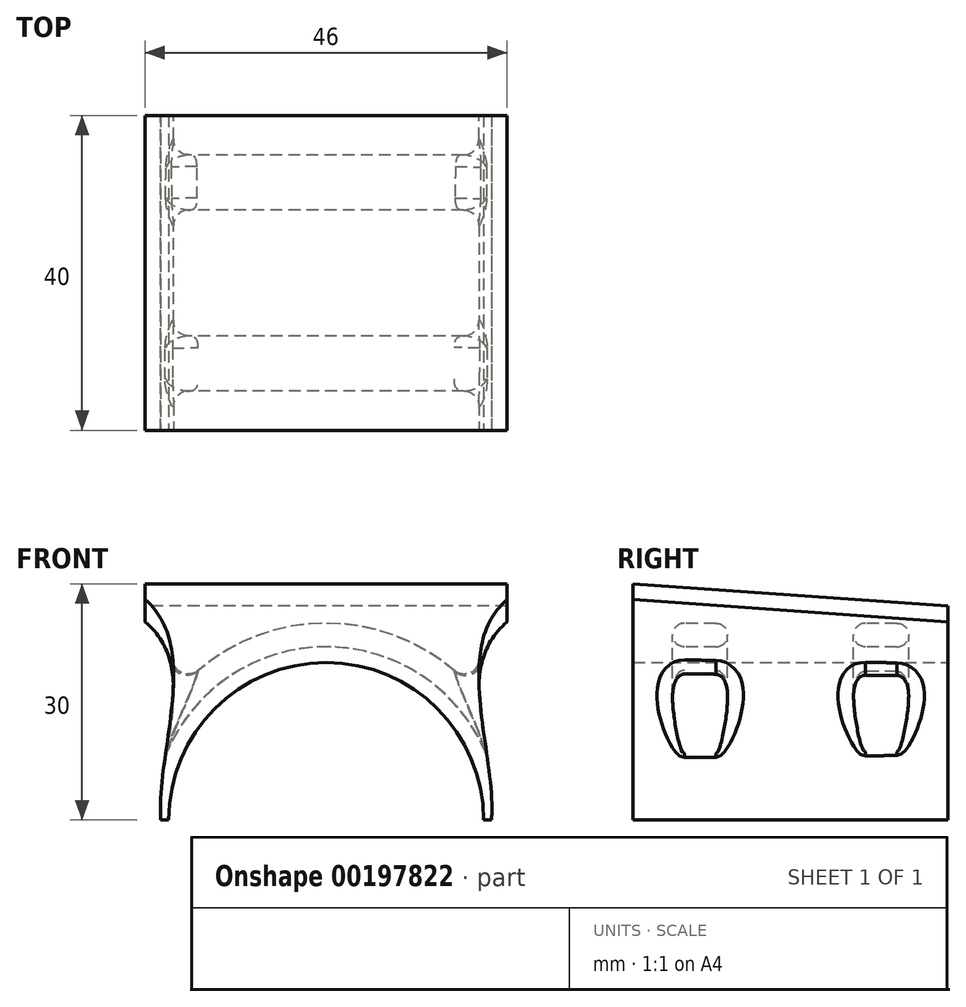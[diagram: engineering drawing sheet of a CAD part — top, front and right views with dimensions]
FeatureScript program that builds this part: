
annotation { "Feature Type Name" : "Feature", "Feature Type Description" : "" }
export const myFeature = defineFeature(function(context is Context, id is Id, definition is map)
    precondition{}
    {
        {
            var Q0;
            Q0=qCreatedBy(makeId("Front.planeOp"),FACE);
            var sketch = newSketch(context, id + "F0", { "sketchPlane" : qUnion([Q0])});
            skArc(sketch, "E0", {"start": v(20, 0) * mm, "mid": v(0, 20) * mm, "end": v(-20, 0) * mm});
            skLineSegment(sketch, "E1.top", {"start": v(23, 27.19) * mm, "end": v(-23, 27.19) * mm});
            skLineSegment(sketch, "E1.left", {"start": v(23, 25.19) * mm, "end": v(23, 27.19) * mm});
            skLineSegment(sketch, "E1.right", {"start": v(-23, 25.19) * mm, "end": v(-23, 27.19) * mm});
            skFitSpline(sketch, "E2", {"points": [v(-23, 25.19) * mm, v(-21, 0) * mm], "startDerivative": vector(21.52, -17.98) * mm, "endDerivative": vector(2, -25.19) * mm});
            skFitSpline(sketch, "E3.MirrorCS", {"points": [v(23, 25.19) * mm, v(21, 0) * mm], "startDerivative": vector(-21.52, -17.98) * mm, "endDerivative": vector(-2, -25.19) * mm});
            skLineSegment(sketch, "E4", {"start": v(-21, 0) * mm, "end": v(-20, 0) * mm});
            skLineSegment(sketch, "E5", {"start": v(20, 0) * mm, "end": v(21, 0) * mm});
            skSolve(sketch);
        }
        {
            var Q0;
            Q0=qCreatedBy(makeId("Front.planeOp"),FACE);
            cPlane(context, id + "F1", {"entities" : qUnion([Q0]), "cplaneType" : CPlaneType.OFFSET, "offset" : 40 * mm, "width" : 150 * mm, "height" : 150 * mm});
        }
        {
            var Q0;
            Q0=qCreatedBy(id+"F1.planeOp",FACE);
            var sketch = newSketch(context, id + "F2", { "sketchPlane" : qUnion([Q0])});
            skArc(sketch, "E6", {"start": v(20, 0) * mm, "mid": v(0, 20) * mm, "end": v(-20, 0) * mm});
            skLineSegment(sketch, "E7.top", {"start": v(23, 30) * mm, "end": v(-23, 30) * mm});
            skLineSegment(sketch, "E7.right", {"start": v(-23, 28) * mm, "end": v(-23, 30) * mm});
            skFitSpline(sketch, "E8", {"points": [v(-23, 28) * mm, v(-21, 0) * mm], "startDerivative": vector(21.52, -17.98) * mm, "endDerivative": vector(2, -25.19) * mm});
            skLineSegment(sketch, "E9", {"start": v(-21, 0) * mm, "end": v(-20, 0) * mm});
            skLineSegment(sketch, "E10", {"start": v(20, 0) * mm, "end": v(21, 0) * mm});
            skLineSegment(sketch, "E11.MirrorCS", {"start": v(23, 28) * mm, "end": v(23, 30) * mm});
            skFitSpline(sketch, "E12.MirrorCS", {"points": [v(23, 28) * mm, v(21, 0) * mm], "startDerivative": vector(-21.52, -17.98) * mm, "endDerivative": vector(-2, -25.19) * mm});
            skSolve(sketch);
        }
        {
            var Q0;
            Q0 = qSketchRegion(id + "F0", true);
            var Q1;
            Q1 = qSketchRegion(id + "F2", true);
            loft(context, id + "F3", {"sheetProfilesArray" : [{ "sheetProfileEntities" : qUnion([Q0]) }, { "sheetProfileEntities" : qUnion([Q1]) }]});
        }
        {
            var Q0;
            Q0=qCreatedBy(makeId("Right.planeOp"),FACE);
            var sketch = newSketch(context, id + "F4", { "sketchPlane" : qUnion([Q0])});
            skLineSegment(sketch, "E13.bottom", {"start": v(-6.5, 22) * mm, "end": v(-10.5, 22) * mm});
            skLineSegment(sketch, "E13.top", {"start": v(-6.5, 25) * mm, "end": v(-10.5, 25) * mm});
            skLineSegment(sketch, "E13.left", {"start": v(-5, 23.5) * mm, "end": v(-5, 23.5) * mm});
            skLineSegment(sketch, "E13.right", {"start": v(-12, 23.5) * mm, "end": v(-12, 23.5) * mm});
            skPoint(sketch, "E13.middle", {"position": v(-8.5, 23.5) * mm});
            skLineSegment(sketch, "E14", {"start": v(-20, 15.77) * mm, "end": v(-20, -8.13) * mm, "construction": true});
            skPoint(sketch, "E15.MirrorP", {"position": v(-31.5, 23.5) * mm});
            skLineSegment(sketch, "E16.MirrorCS", {"start": v(-33.5, 25) * mm, "end": v(-29.5, 25) * mm});
            skLineSegment(sketch, "E17.MirrorCS", {"start": v(-28, 23.5) * mm, "end": v(-28, 23.5) * mm});
            skLineSegment(sketch, "E18.MirrorCS", {"start": v(-35, 23.5) * mm, "end": v(-35, 23.5) * mm});
            skLineSegment(sketch, "E19.MirrorCS", {"start": v(-33.5, 22) * mm, "end": v(-29.5, 22) * mm});
            skPoint(sketch, "E20.visualSharp", {"position": v(-5, 22) * mm});
            skArc(sketch, "E20.filletArc", {"start": v(-6.5, 22) * mm, "mid": v(-5.44, 22.44) * mm, "end": v(-5, 23.5) * mm});
            skPoint(sketch, "E21.visualSharp", {"position": v(-5, 25) * mm});
            skArc(sketch, "E21.filletArc", {"start": v(-5, 23.5) * mm, "mid": v(-5.44, 24.56) * mm, "end": v(-6.5, 25) * mm});
            skPoint(sketch, "E22.visualSharp", {"position": v(-12, 25) * mm});
            skArc(sketch, "E22.filletArc", {"start": v(-10.5, 25) * mm, "mid": v(-11.56, 24.56) * mm, "end": v(-12, 23.5) * mm});
            skPoint(sketch, "E23.visualSharp", {"position": v(-12, 22) * mm});
            skArc(sketch, "E23.filletArc", {"start": v(-12, 23.5) * mm, "mid": v(-11.56, 22.44) * mm, "end": v(-10.5, 22) * mm});
            skPoint(sketch, "E24.visualSharp", {"position": v(-35, 22) * mm});
            skArc(sketch, "E24.filletArc", {"start": v(-35, 23.5) * mm, "mid": v(-34.56, 22.44) * mm, "end": v(-33.5, 22) * mm});
            skPoint(sketch, "E25.visualSharp", {"position": v(-35, 25) * mm});
            skArc(sketch, "E25.filletArc", {"start": v(-33.5, 25) * mm, "mid": v(-34.56, 24.56) * mm, "end": v(-35, 23.5) * mm});
            skPoint(sketch, "E26.visualSharp", {"position": v(-28, 25) * mm});
            skArc(sketch, "E26.filletArc", {"start": v(-28, 23.5) * mm, "mid": v(-28.44, 24.56) * mm, "end": v(-29.5, 25) * mm});
            skPoint(sketch, "E27.visualSharp", {"position": v(-28, 22) * mm});
            skArc(sketch, "E27.filletArc", {"start": v(-29.5, 22) * mm, "mid": v(-28.44, 22.44) * mm, "end": v(-28, 23.5) * mm});
            skSolve(sketch);
        }
        {
            var Q0;
            Q0=qCreatedBy(makeId("Right.planeOp"),FACE);
            var sketch = newSketch(context, id + "F5", { "sketchPlane" : qUnion([Q0])});
            skLineSegment(sketch, "E28", {"start": v(0, 0) * mm, "end": v(-40.86, 0) * mm, "construction": true});
            skSolve(sketch);
        }
        {
            var Q0;
            Q0 = qSketchRegion(id + "F4", true);
            var Q1;
            Q1=sQuery(id+"F5.wireOp",EDGE,"E28");
            revolve(context, id + "F6", {"operationType" : NewBodyOperationType.REMOVE, "entities" : qUnion([Q0]), "axis" : qUnion([Q1]), "revolveType" : RevolveType.FULL, "oppositeDirection" : true});
        }
        {
            var Q0;
            Q0=makeQuery(id+"F6.boolean.opBoolean","INTERSECT",EDGE,{"derivedFrom":[makeQuery(id+"F3.opLoft","SWEPT_FACE",FACE,{"disambiguationData":[OSD([sQuery(id+"F0.wireOp",EDGE,"E1.left"),sQuery(id+"F0.wireOp",EDGE,"E3.MirrorCS"),sQuery(id+"F0.wireOp",EDGE,"E5"),sQuery(id+"F2.wireOp",EDGE,"E10"),sQuery(id+"F2.wireOp",EDGE,"E11.MirrorCS"),sQuery(id+"F2.wireOp",EDGE,"E12.MirrorCS")])]}),makeQuery(id+"F6.opRevolve","SWEPT_FACE",FACE,{"disambiguationData":[OSD([sQuery(id+"F4.wireOp",EDGE,"E16.MirrorCS")])]})]});
            var Q1;
            Q1=makeQuery(id+"F6.boolean.opBoolean","INTERSECT",EDGE,{"derivedFrom":[makeQuery(id+"F3.opLoft","SWEPT_FACE",FACE,{"disambiguationData":[OSD([sQuery(id+"F0.wireOp",EDGE,"E1.left"),sQuery(id+"F0.wireOp",EDGE,"E3.MirrorCS"),sQuery(id+"F0.wireOp",EDGE,"E5"),sQuery(id+"F2.wireOp",EDGE,"E10"),sQuery(id+"F2.wireOp",EDGE,"E11.MirrorCS"),sQuery(id+"F2.wireOp",EDGE,"E12.MirrorCS")])]}),makeQuery(id+"F6.opRevolve","SWEPT_FACE",FACE,{"disambiguationData":[OSD([sQuery(id+"F4.wireOp",EDGE,"E13.top")])]})]});
            var Q2;
            Q2=makeQuery(id+"F6.boolean.opBoolean","INTERSECT",EDGE,{"derivedFrom":[makeQuery(id+"F3.opLoft","SWEPT_FACE",FACE,{"disambiguationData":[OSD([sQuery(id+"F0.wireOp",EDGE,"E1.right"),sQuery(id+"F0.wireOp",EDGE,"E2"),sQuery(id+"F0.wireOp",EDGE,"E4"),sQuery(id+"F2.wireOp",EDGE,"E7.right"),sQuery(id+"F2.wireOp",EDGE,"E8"),sQuery(id+"F2.wireOp",EDGE,"E9")])]}),makeQuery(id+"F6.opRevolve","SWEPT_FACE",FACE,{"disambiguationData":[OSD([sQuery(id+"F4.wireOp",EDGE,"E13.top")])]})]});
            var Q3;
            Q3=makeQuery(id+"F6.boolean.opBoolean","INTERSECT",EDGE,{"derivedFrom":[makeQuery(id+"F3.opLoft","SWEPT_FACE",FACE,{"disambiguationData":[OSD([sQuery(id+"F0.wireOp",EDGE,"E1.right"),sQuery(id+"F0.wireOp",EDGE,"E2"),sQuery(id+"F0.wireOp",EDGE,"E4"),sQuery(id+"F2.wireOp",EDGE,"E7.right"),sQuery(id+"F2.wireOp",EDGE,"E8"),sQuery(id+"F2.wireOp",EDGE,"E9")])]}),makeQuery(id+"F6.opRevolve","SWEPT_FACE",FACE,{"disambiguationData":[OSD([sQuery(id+"F4.wireOp",EDGE,"E16.MirrorCS")])]})]});
            fillet(context, id + "F7", {"entities" : qUnion([Q0, Q1, Q2, Q3]), "radius" : 2 * mm, "tangentPropagation" : true, "allowEdgeOverflow" : false});
        }
    });
